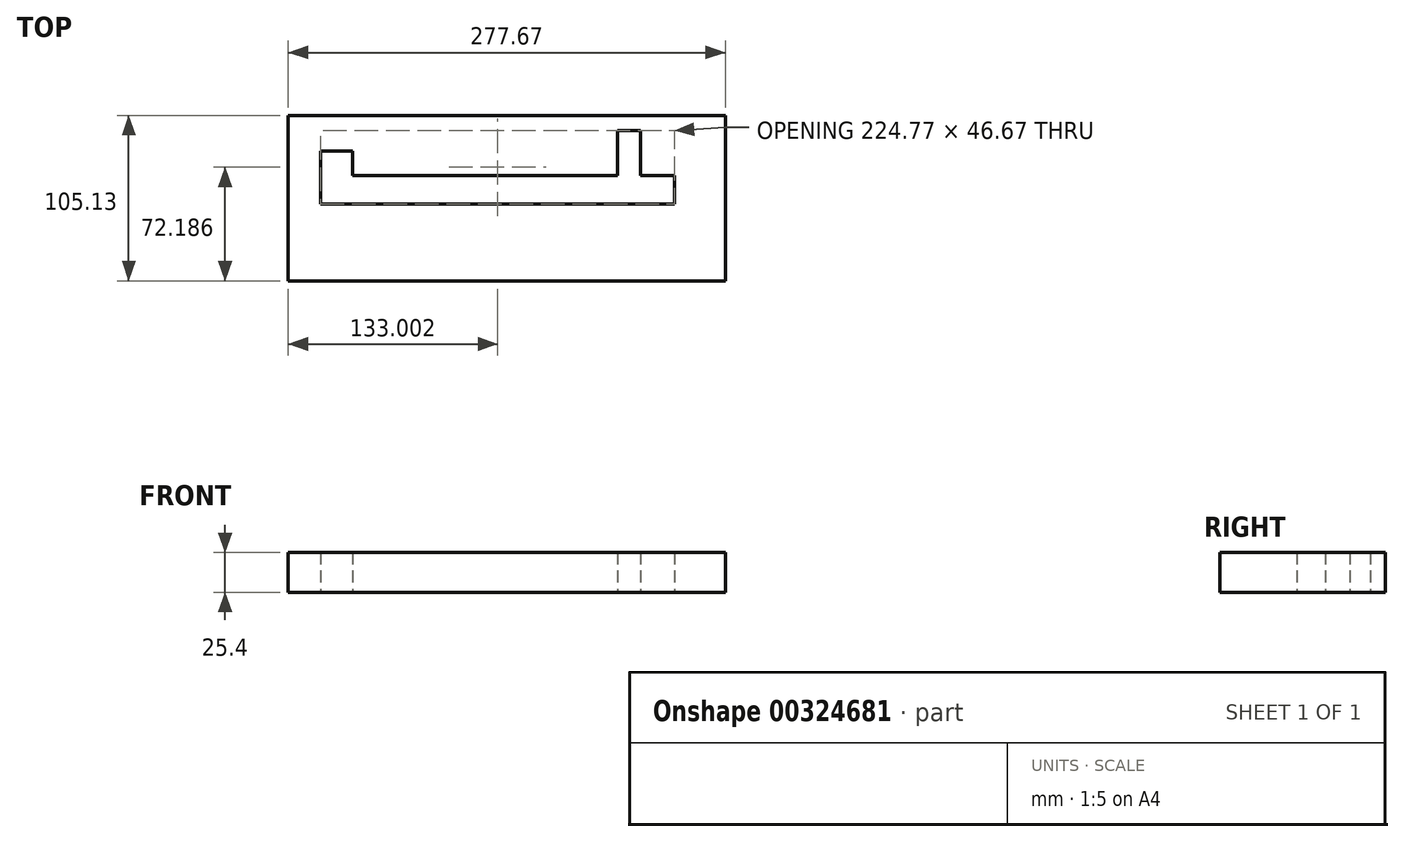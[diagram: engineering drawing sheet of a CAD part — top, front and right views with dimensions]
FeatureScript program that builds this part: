
annotation { "Feature Type Name" : "Feature", "Feature Type Description" : "" }
export const myFeature = defineFeature(function(context is Context, id is Id, definition is map)
    precondition{}
    {
        {
            var Q0;
            Q0=qCreatedBy(makeId("Top.planeOp"),FACE);
            var sketch = newSketch(context, id + "F0", { "sketchPlane" : qUnion([Q0])});
            skLineSegment(sketch, "E0.bottom", {"start": v(-140.4, 56.28) * mm, "end": v(137.27, 56.28) * mm});
            skLineSegment(sketch, "E0.top", {"start": v(-140.4, -48.85) * mm, "end": v(137.27, -48.85) * mm});
            skLineSegment(sketch, "E0.left", {"start": v(-140.4, 56.28) * mm, "end": v(-140.4, -48.85) * mm});
            skLineSegment(sketch, "E0.right", {"start": v(137.27, 56.28) * mm, "end": v(137.27, -48.85) * mm});
            skLineSegment(sketch, "E1.bottom", {"start": v(-99.56, 0) * mm, "end": v(-119.78, 0) * mm});
            skLineSegment(sketch, "E1.top", {"start": v(-99.56, 33.56) * mm, "end": v(-119.78, 33.56) * mm});
            skLineSegment(sketch, "E1.left", {"start": v(-99.56, 0) * mm, "end": v(-99.56, 33.56) * mm});
            skLineSegment(sketch, "E1.right", {"start": v(-119.78, 0) * mm, "end": v(-119.78, 33.56) * mm});
            skLineSegment(sketch, "E2.bottom", {"start": v(-110.79, 17.98) * mm, "end": v(104.99, 17.98) * mm});
            skLineSegment(sketch, "E2.top", {"start": v(-110.79, 0) * mm, "end": v(104.99, 0) * mm});
            skLineSegment(sketch, "E2.left", {"start": v(-110.79, 17.98) * mm, "end": v(-110.79, 0) * mm});
            skLineSegment(sketch, "E2.right", {"start": v(104.99, 17.98) * mm, "end": v(104.99, 0) * mm});
            skLineSegment(sketch, "E3.bottom", {"start": v(83.2, 8.8) * mm, "end": v(68.85, 8.8) * mm});
            skLineSegment(sketch, "E3.top", {"start": v(83.2, 46.67) * mm, "end": v(68.85, 46.67) * mm});
            skLineSegment(sketch, "E3.left", {"start": v(83.2, 8.8) * mm, "end": v(83.2, 46.67) * mm});
            skLineSegment(sketch, "E3.right", {"start": v(68.85, 8.8) * mm, "end": v(68.85, 46.67) * mm});
            skSolve(sketch);
        }
        {
            var Q0;
            Q0=makeQuery(id+"F0.imprint","IMPRINT",FACE,{"disambiguationData":[TD([[makeQuery(id+"F0.imprint","IMPRINT",EDGE,{"derivedFrom":sQuery(id+"F0.wireOp",EDGE,"E0.bottom")}),-1.0]])]});
            extrude(context, id + "F1", {"entities" : qUnion([Q0]), "depth" : 25.4 * mm});
        }
    });
